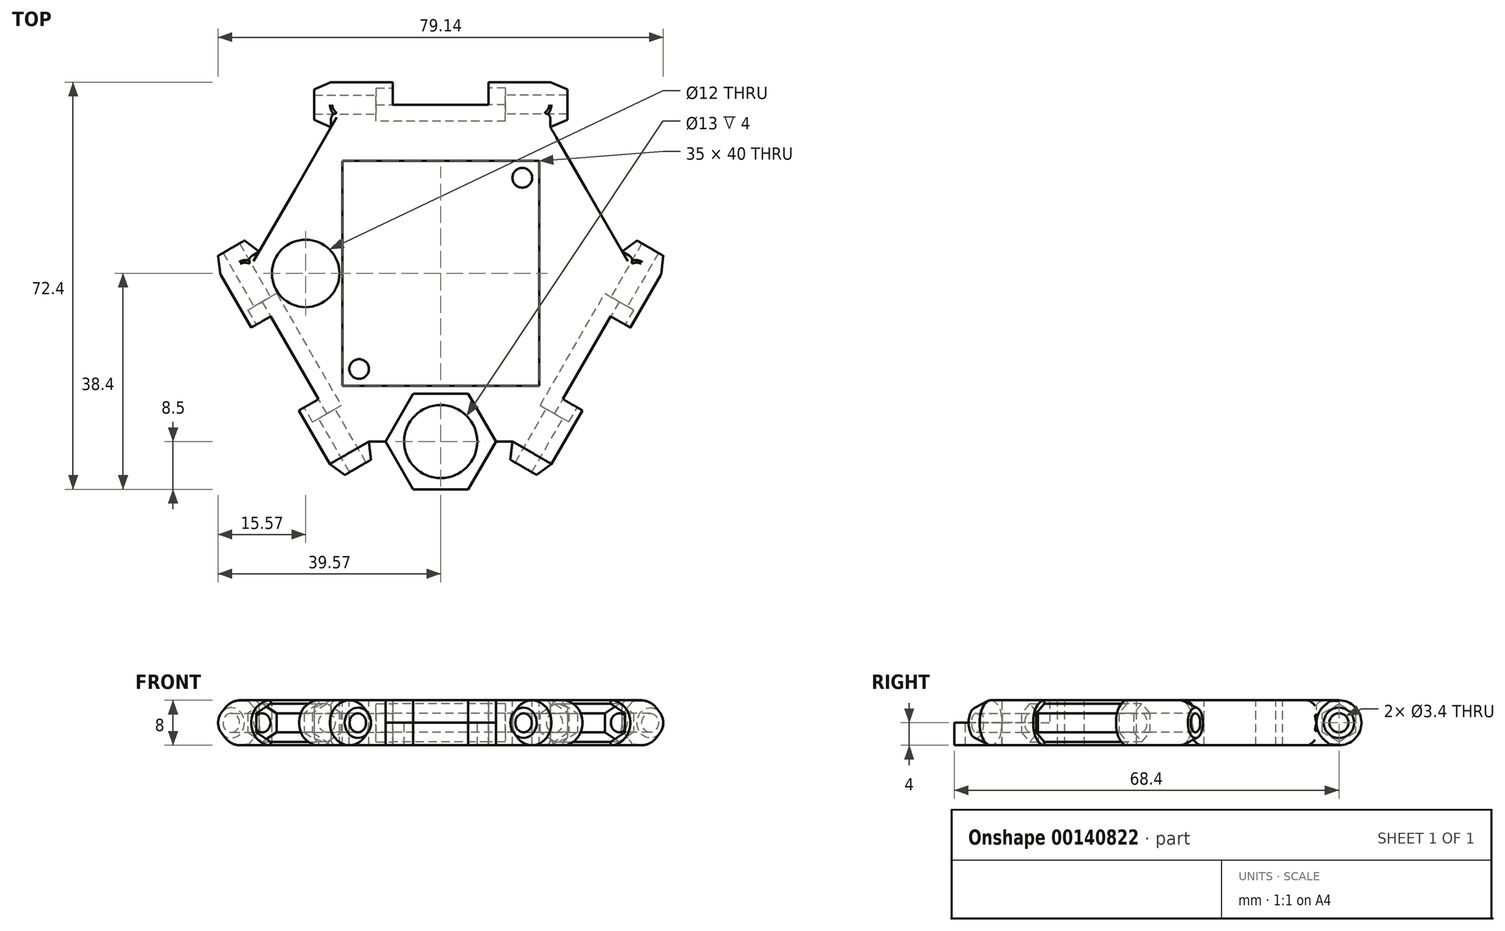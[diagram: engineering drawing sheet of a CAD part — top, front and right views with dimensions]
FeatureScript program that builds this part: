
annotation { "Feature Type Name" : "Feature", "Feature Type Description" : "" }
export const myFeature = defineFeature(function(context is Context, id is Id, definition is map)
    precondition{}
    {
        {
            var Q0;
            Q0=qCreatedBy(makeId("Top.planeOp"),FACE);
            var sketch = newSketch(context, id + "F0", { "sketchPlane" : qUnion([Q0])});
            skLineSegment(sketch, "E0.top", {"start": v(0, 34) * mm, "end": v(19.5, 34) * mm});
            skLineSegment(sketch, "E1", {"start": v(22.5, 31.7) * mm, "end": v(22.5, 32.7) * mm});
            skLineSegment(sketch, "E2", {"start": v(19.5, 34) * mm, "end": v(22.5, 32.7) * mm});
            skLineSegment(sketch, "E3", {"start": v(22.5, 31.7) * mm, "end": v(0, 31.7) * mm});
            skPoint(sketch, "E4.0.midPoint", {"position": v(0, 30) * mm});
            skLineSegment(sketch, "E5", {"start": v(19.5, 30) * mm, "end": v(36.82, 0) * mm, "construction": true});
            skLineSegment(sketch, "E6", {"start": v(0, 0) * mm, "end": v(27.62, 15.94) * mm, "construction": true});
            skLineSegment(sketch, "E7", {"start": v(0, 30) * mm, "end": v(22.5, 30) * mm, "construction": true});
            skLineSegment(sketch, "E8", {"start": v(0, 0) * mm, "end": v(0, 34) * mm});
            skLineSegment(sketch, "E9.MirrorCS", {"start": v(22.5, 28.3) * mm, "end": v(0, 28.3) * mm});
            skLineSegment(sketch, "E10.MirrorCS", {"start": v(0, 26) * mm, "end": v(19.5, 26) * mm});
            skLineSegment(sketch, "E11.MirrorCS", {"start": v(22.5, 28.3) * mm, "end": v(22.5, 27.3) * mm});
            skLineSegment(sketch, "E12.MirrorCS", {"start": v(19.5, 26) * mm, "end": v(22.5, 27.3) * mm});
            skLineSegment(sketch, "E13", {"start": v(19.5, 26) * mm, "end": v(32.2, 4) * mm, "construction": true});
            skLineSegment(sketch, "E14", {"start": v(0, 0) * mm, "end": v(25.88, 14.94) * mm});
            skLineSegment(sketch, "E15", {"start": v(19.5, 26) * mm, "end": v(25.88, 14.94) * mm});
            skSolve(sketch);
        }
        {
            var Q0;
            Q0=qCreatedBy(makeId("Right.planeOp"),FACE);
            var sketch = newSketch(context, id + "F1", { "sketchPlane" : qUnion([Q0])});
            skCircle(sketch, "E16.cCircle", {"center": v(30, 0) * mm, "radius": 2.95 * mm, "construction": true});
            skLineSegment(sketch, "E16.0", {"start": v(32.95, -1.7) * mm, "end": v(30, -3.4) * mm});
            skLineSegment(sketch, "E16.1", {"start": v(30, -3.4) * mm, "end": v(27.05, -1.7) * mm});
            skLineSegment(sketch, "E16.2", {"start": v(27.05, -1.7) * mm, "end": v(27.05, 1.7) * mm});
            skLineSegment(sketch, "E16.3", {"start": v(27.05, 1.7) * mm, "end": v(30, 3.4) * mm});
            skLineSegment(sketch, "E16.4", {"start": v(30, 3.4) * mm, "end": v(32.95, 1.7) * mm});
            skLineSegment(sketch, "E16.5", {"start": v(32.95, 1.7) * mm, "end": v(32.95, -1.7) * mm});
            skCircle(sketch, "E17", {"center": v(30, 0) * mm, "radius": 4 * mm});
            skLineSegment(sketch, "E18", {"start": v(26, 0) * mm, "end": v(26, -4) * mm});
            skLineSegment(sketch, "E19", {"start": v(26, -4) * mm, "end": v(30, -4) * mm});
            skLineSegment(sketch, "E20", {"start": v(30, 4) * mm, "end": v(30, -4) * mm, "construction": true});
            skLineSegment(sketch, "E21.MirrorCS", {"start": v(26, 4) * mm, "end": v(30, 4) * mm});
            skLineSegment(sketch, "E22.MirrorCS", {"start": v(26, 0) * mm, "end": v(26, 4) * mm});
            skLineSegment(sketch, "E23", {"start": v(0, 4) * mm, "end": v(0, -4) * mm, "construction": true});
            skLineSegment(sketch, "E24", {"start": v(30, 4) * mm, "end": v(30, 3.4) * mm});
            skLineSegment(sketch, "E25", {"start": v(30, -3.4) * mm, "end": v(30, -4) * mm});
            skSolve(sketch);
        }
        {
            var Q0;
            Q0=qCreatedBy(makeId("Top.planeOp"),FACE);
            var sketch = newSketch(context, id + "F2", { "sketchPlane" : qUnion([Q0])});
            skCircle(sketch, "E26.MirrorC", {"center": v(14.5, 17) * mm, "radius": 1.75 * mm});
            skLineSegment(sketch, "E27", {"start": v(0, 20) * mm, "end": v(17.5, 20) * mm, "construction": true});
            skLineSegment(sketch, "E28", {"start": v(17.5, 20) * mm, "end": v(17.5, 0) * mm, "construction": true});
            skLineSegment(sketch, "E29", {"start": v(17.5, 20) * mm, "end": v(0, 0) * mm, "construction": true});
            skCircle(sketch, "E30", {"center": v(10, 10) * mm, "radius": 4 * mm, "construction": true});
            skLineSegment(sketch, "E31", {"start": v(0, 10) * mm, "end": v(17.5, 10) * mm, "construction": true});
            skFitSpline(sketch, "E32", {"points": [v(12.53, 14.32) * mm, v(14.26, 12.62) * mm, v(15, 10) * mm], "startDerivative": vector(4.86, -2.41) * mm, "endDerivative": vector(0.41, -5.85) * mm});
            skLineSegment(sketch, "E33", {"start": v(15, 10) * mm, "end": v(15, 0) * mm});
            skLineSegment(sketch, "E34", {"start": v(12.53, 14.32) * mm, "end": v(2.46, 16.87) * mm});
            skLineSegment(sketch, "E35.MirrorCS", {"start": v(-12.53, 14.32) * mm, "end": v(-2.46, 16.87) * mm});
            skFitSpline(sketch, "E36.MirrorCS", {"points": [v(-12.53, 14.32) * mm, v(-14.26, 12.62) * mm, v(-15, 10) * mm], "startDerivative": vector(-4.86, -2.41) * mm, "endDerivative": vector(-0.41, -5.85) * mm});
            skLineSegment(sketch, "E37.MirrorCS", {"start": v(-15, 10) * mm, "end": v(-15, 0) * mm});
            skCircle(sketch, "E38.MirrorC", {"center": v(-14.5, 17) * mm, "radius": 1.75 * mm});
            skPoint(sketch, "E39.visualSharp", {"position": v(0, 17.5) * mm});
            skArc(sketch, "E39.filletArc", {"start": v(2.46, 16.87) * mm, "mid": v(0, 17.18) * mm, "end": v(-2.46, 16.87) * mm});
            skCircle(sketch, "E40.MirrorC", {"center": v(-14.5, -17) * mm, "radius": 1.75 * mm});
            skCircle(sketch, "E41.MirrorC", {"center": v(14.5, -17) * mm, "radius": 1.75 * mm});
            skLineSegment(sketch, "E42.MirrorCS", {"start": v(15, -10) * mm, "end": v(15, 0) * mm});
            skFitSpline(sketch, "E43.MirrorCS", {"points": [v(12.53, -14.32) * mm, v(14.26, -12.62) * mm, v(15, -10) * mm], "startDerivative": vector(4.86, 2.41) * mm, "endDerivative": vector(0.41, 5.85) * mm});
            skLineSegment(sketch, "E44.MirrorCS", {"start": v(12.53, -14.32) * mm, "end": v(2.46, -16.87) * mm});
            skArc(sketch, "E45.MirrorCS", {"start": v(2.46, -16.87) * mm, "mid": v(0, -17.18) * mm, "end": v(-2.46, -16.87) * mm});
            skLineSegment(sketch, "E46.MirrorCS", {"start": v(-12.53, -14.32) * mm, "end": v(-2.46, -16.87) * mm});
            skLineSegment(sketch, "E47.MirrorCS", {"start": v(-15, -10) * mm, "end": v(-15, 0) * mm});
            skFitSpline(sketch, "E48.MirrorCS", {"points": [v(-12.53, -14.32) * mm, v(-14.26, -12.62) * mm, v(-15, -10) * mm], "startDerivative": vector(-4.86, 2.41) * mm, "endDerivative": vector(-0.41, 5.85) * mm});
            skLineSegment(sketch, "E49.bottom", {"start": v(-17.5, 20) * mm, "end": v(17.5, 20) * mm});
            skLineSegment(sketch, "E49.top", {"start": v(-17.5, -20) * mm, "end": v(17.5, -20) * mm});
            skLineSegment(sketch, "E49.left", {"start": v(-17.5, 20) * mm, "end": v(-17.5, -20) * mm});
            skLineSegment(sketch, "E49.right", {"start": v(17.5, 20) * mm, "end": v(17.5, -20) * mm});
            skPoint(sketch, "E49.middle", {"position": v(0, 0) * mm});
            skCircle(sketch, "E50", {"center": v(-24, 0) * mm, "radius": 6 * mm});
            skCircle(sketch, "E51.MirrorC", {"center": v(24, 0) * mm, "radius": 6 * mm});
            skSolve(sketch);
        }
        {
            var Q0;
            {var subQ1=sQuery(id+"F0.wireOp",EDGE,"E0.top");Q0=makeQuery(id+"F0.imprint","IMPRINT",FACE,{"disambiguationData":[TD([[makeQuery(id+"F0.imprint","IMPRINT",EDGE,{"derivedFrom":subQ1}),-1.0]])]});}
            var Q1;
            Q1=sQuery(id+"F0.wireOp",EDGE,"E7");
            revolve(context, id + "F3", {"entities" : qUnion([Q0]), "axis" : qUnion([Q1]), "revolveType" : RevolveType.FULL});
        }
        {
            var Q0;
            {var subQ2=sQuery(id+"F1.wireOp",EDGE,"E21.MirrorCS");Q0=makeQuery(id+"F1.imprint","IMPRINT",FACE,{"disambiguationData":[TD([[makeQuery(id+"F1.imprint","IMPRINT",EDGE,{"derivedFrom":subQ2}),-1.0]])]});}
            var Q1;
            {var subQ0=sQuery(id+"F1.wireOp",EDGE,"E18");Q1=makeQuery(id+"F1.imprint","IMPRINT",FACE,{"disambiguationData":[TD([[makeQuery(id+"F1.imprint","IMPRINT",EDGE,{"derivedFrom":subQ0}),1.0]])]});}
            var Q2;
            {var subQ0=sQuery(id+"F1.wireOp",EDGE,"E19");var subQ1=sQuery(id+"F1.wireOp",EDGE,"E17");var subQ2=makeQuery(id+"F1.imprint","INTERSECT",VERTEX,{"derivedFrom":[subQ1,subQ0]});Q2=makeQuery(id+"F1.imprint","IMPRINT",FACE,{"disambiguationData":[TD([[makeQuery(id+"F1.imprint","IMPRINT",EDGE,{"disambiguationData":[TD([[subQ2,1.0]])],"derivedFrom":subQ1}),-1.0]])]});}
            var Q3;
            {var subQ0=sQuery(id+"F1.wireOp",EDGE,"E22.MirrorCS");Q3=makeQuery(id+"F1.imprint","IMPRINT",FACE,{"disambiguationData":[TD([[makeQuery(id+"F1.imprint","IMPRINT",EDGE,{"derivedFrom":subQ0}),-1.0]])]});}
            extrude(context, id + "F4", {"entities" : qUnion([Q0, Q1, Q2, Q3]), "operationType" : NewBodyOperationType.ADD, "depth" : 19.5 * mm});
        }
        {
            var Q0;
            {var subQ2=sQuery(id+"F0.wireOp",EDGE,"E10.MirrorCS");Q0=makeQuery(id+"F0.imprint","IMPRINT",FACE,{"disambiguationData":[TD([[makeQuery(id+"F0.imprint","IMPRINT",EDGE,{"derivedFrom":subQ2}),-1.0]])]});}
            extrude(context, id + "F5", {"entities" : qUnion([Q0]), "operationType" : NewBodyOperationType.ADD, "endBound" : BoundingType.SYMMETRIC, "depth" : 8 * mm});
        }
        {
            var Q0;
            Q0=makeQuery(id+"F1.imprint","IMPRINT",FACE,{"disambiguationData":[TD([[makeQuery(id+"F1.imprint","IMPRINT",EDGE,{"derivedFrom":sQuery(id+"F1.wireOp",EDGE,"E16.0")}),-1.0]])]});
            extrude(context, id + "F6", {"entities" : qUnion([Q0]), "operationType" : NewBodyOperationType.REMOVE, "depth" : (45 / 2 - 11) * mm});
        }
        {
            var Q0;
            Q0=makeQuery(id+"F1.imprint","IMPRINT",FACE,{"disambiguationData":[TD([[makeQuery(id+"F1.imprint","IMPRINT",EDGE,{"derivedFrom":sQuery(id+"F1.wireOp",EDGE,"E16.0")}),1.0]])]});
            extrude(context, id + "F7", {"entities" : qUnion([Q0]), "operationType" : NewBodyOperationType.REMOVE, "depth" : (45 / 2 - 14) * mm});
        }
        {
            var Q0;
            Q0=makeQuery(id+"F3.opRevolve","SWEPT_BODY",BODY,{"disambiguationData":[OSD([sQuery(id+"F0.wireOp",EDGE,"E0.top"),sQuery(id+"F0.wireOp",EDGE,"E0.left"),sQuery(id+"F0.wireOp",EDGE,"E1"),sQuery(id+"F0.wireOp",EDGE,"E2"),sQuery(id+"F0.wireOp",EDGE,"E3")])]});
            var Q1;
            Q1=qCreatedBy(makeId("Right.planeOp"),FACE);
            mirror(context, id + "F8", {"operationType" : NewBodyOperationType.ADD, "entities" : qUnion([Q0]), "mirrorPlane" : qUnion([Q1])});
        }
        {
            var Q0;
            Q0=makeQuery(id+"F3.opRevolve","SWEPT_BODY",BODY,{"disambiguationData":[OSD([sQuery(id+"F0.wireOp",EDGE,"E0.top"),sQuery(id+"F0.wireOp",EDGE,"E0.left"),sQuery(id+"F0.wireOp",EDGE,"E1"),sQuery(id+"F0.wireOp",EDGE,"E2"),sQuery(id+"F0.wireOp",EDGE,"E3")])]});
            var Q1;
            Q1=makeQuery(id+"F3.opRevolve","SWEPT_BODY",BODY,{"disambiguationData":[OSD([sQuery(id+"F0.wireOp",EDGE,"E8"),sQuery(id+"F0.wireOp",EDGE,"E9.MirrorCS"),sQuery(id+"F0.wireOp",EDGE,"E10.MirrorCS"),sQuery(id+"F0.wireOp",EDGE,"E11.MirrorCS"),sQuery(id+"F0.wireOp",EDGE,"E12.MirrorCS")])]});
            var Q2;
            Q2=sQuery(id+"F1.wireOp",EDGE,"E23");
            circularPattern(context, id + "F9", {"operationType" : NewBodyOperationType.ADD, "entities" : qUnion([Q0, Q1]), "axis" : qUnion([Q2]), "angle" : 120 * degree, "instanceCount" : 3});
        }
        {
            var Q0;
            Q0=makeQuery(id+"F2.imprint","IMPRINT",FACE,{"disambiguationData":[TD([[makeQuery(id+"F2.imprint","IMPRINT",EDGE,{"derivedFrom":sQuery(id+"F2.wireOp",EDGE,"E32")}),-1.0]])]});
            var Q1;
            Q1=makeQuery(id+"F2.imprint","IMPRINT",FACE,{"disambiguationData":[TD([[makeQuery(id+"F2.imprint","IMPRINT",EDGE,{"derivedFrom":sQuery(id+"F2.wireOp",EDGE,"E38.MirrorC")}),1.0]])]});
            var Q2;
            Q2=makeQuery(id+"F2.imprint","IMPRINT",FACE,{"disambiguationData":[TD([[makeQuery(id+"F2.imprint","IMPRINT",EDGE,{"derivedFrom":sQuery(id+"F2.wireOp",EDGE,"E26.MirrorC")}),-1.0]])]});
            var Q3;
            Q3=makeQuery(id+"F2.imprint","IMPRINT",FACE,{"disambiguationData":[TD([[makeQuery(id+"F2.imprint","IMPRINT",EDGE,{"derivedFrom":sQuery(id+"F2.wireOp",EDGE,"E41.MirrorC")}),1.0]])]});
            var Q4;
            Q4=makeQuery(id+"F2.imprint","IMPRINT",FACE,{"disambiguationData":[TD([[makeQuery(id+"F2.imprint","IMPRINT",EDGE,{"derivedFrom":sQuery(id+"F2.wireOp",EDGE,"E40.MirrorC")}),-1.0]])]});
            var Q5;
            Q5=makeQuery(id+"F2.imprint","IMPRINT",FACE,{"disambiguationData":[TD([[makeQuery(id+"F2.imprint","IMPRINT",EDGE,{"derivedFrom":sQuery(id+"F2.wireOp",EDGE,"E50")}),1.0]])]});
            var Q6;
            Q6=makeQuery(id+"F2.imprint","IMPRINT",FACE,{"disambiguationData":[TD([[makeQuery(id+"F2.imprint","IMPRINT",EDGE,{"derivedFrom":sQuery(id+"F2.wireOp",EDGE,"E51.MirrorC")}),-1.0]])]});
            var Q7;
            {var subQ0=sQuery(id+"F2.wireOp",EDGE,"E50");var subQ1=sQuery(id+"F2.wireOp",EDGE,"JJTMQ2RY-KDWr-5WRS-YdwC-lt0RPVDN6D57.right");var subQ2=makeQuery(id+"F2.imprint","INTERSECT",VERTEX,{"disambiguationData":[OD(0.0)],"derivedFrom":[subQ1,subQ0]});Q7=makeQuery(id+"F2.imprint","IMPRINT",FACE,{"disambiguationData":[TD([[makeQuery(id+"F2.imprint","IMPRINT",EDGE,{"disambiguationData":[TD([[subQ2,-1.0]])],"derivedFrom":subQ1}),1.0]])]});}
            var Q8;
            {var subQ0=sQuery(id+"F2.wireOp",EDGE,"E51.MirrorC");var subQ1=sQuery(id+"F2.wireOp",EDGE,"JJTMQ2RY-KDWr-5WRS-YdwC-lt0RPVDN6D57.left");var subQ2=makeQuery(id+"F2.imprint","INTERSECT",VERTEX,{"disambiguationData":[OD(0.0)],"derivedFrom":[subQ1,subQ0]});Q8=makeQuery(id+"F2.imprint","IMPRINT",FACE,{"disambiguationData":[TD([[makeQuery(id+"F2.imprint","IMPRINT",EDGE,{"disambiguationData":[TD([[subQ2,-1.0]])],"derivedFrom":subQ1}),-1.0]])]});}
            extrude(context, id + "F10", {"entities" : qUnion([Q0, Q1, Q2, Q3, Q4, Q5, Q6, Q7, Q8]), "operationType" : NewBodyOperationType.REMOVE, "endBound" : BoundingType.SYMMETRIC, "oppositeDirection" : true, "depth" : 8 * mm});
        }
        {
            var Q0;
            Q0=qCreatedBy(makeId("Top.planeOp"),FACE);
            var sketch = newSketch(context, id + "F11", { "sketchPlane" : qUnion([Q0])});
            skCircle(sketch, "E52.cCircle", {"center": v(0, -29.9) * mm, "radius": 8.5 * mm, "construction": true});
            skLineSegment(sketch, "E52.0", {"start": v(-4.9, -21.4) * mm, "end": v(4.9, -21.4) * mm});
            skLineSegment(sketch, "E52.1", {"start": v(4.9, -21.4) * mm, "end": v(9.81, -29.9) * mm});
            skLineSegment(sketch, "E52.2", {"start": v(9.81, -29.9) * mm, "end": v(4.9, -38.4) * mm});
            skLineSegment(sketch, "E52.3", {"start": v(4.9, -38.4) * mm, "end": v(-4.9, -38.4) * mm});
            skLineSegment(sketch, "E52.4", {"start": v(-4.9, -38.4) * mm, "end": v(-9.81, -29.9) * mm});
            skLineSegment(sketch, "E52.5", {"start": v(-9.81, -29.9) * mm, "end": v(-4.9, -21.4) * mm});
            skPoint(sketch, "E52.0.midPoint", {"position": v(0, -21.4) * mm});
            skCircle(sketch, "E53", {"center": v(0, -29.9) * mm, "radius": 6.5 * mm});
            skCircle(sketch, "E54", {"center": v(0, -29.9) * mm, "radius": 10 * mm});
            skSolve(sketch);
        }
        {
            var Q0;
            Q0=makeQuery(id+"F11.imprint","IMPRINT",FACE,{"disambiguationData":[TD([[makeQuery(id+"F11.imprint","IMPRINT",EDGE,{"derivedFrom":sQuery(id+"F11.wireOp",EDGE,"E53")}),1.0]])]});
            var Q1;
            Q1=makeQuery(id+"F11.imprint","IMPRINT",FACE,{"disambiguationData":[TD([[makeQuery(id+"F11.imprint","IMPRINT",EDGE,{"derivedFrom":sQuery(id+"F11.wireOp",EDGE,"E52.0")}),-1.0]])]});
            extrude(context, id + "F12", {"entities" : qUnion([Q0, Q1]), "operationType" : NewBodyOperationType.REMOVE, "endBound" : BoundingType.SYMMETRIC, "depth" : 40 * mm});
        }
        {
            var Q0;
            Q0=makeQuery(id+"F11.imprint","IMPRINT",FACE,{"disambiguationData":[TD([[makeQuery(id+"F11.imprint","IMPRINT",EDGE,{"derivedFrom":sQuery(id+"F11.wireOp",EDGE,"E52.0")}),-1.0]])]});
            extrude(context, id + "F13", {"entities" : qUnion([Q0]), "operationType" : NewBodyOperationType.ADD, "oppositeDirection" : true, "depth" : 4 * mm});
        }
        {
            var Q0;
            {var subQ0=makeQuery(id+"F5.opExtrude","CAP_EDGE",EDGE,{"disambiguationData":[OSD([sQuery(id+"F0.wireOp",EDGE,"E15")])],"isStart":false});Q0=makeQuery(id+"F9.boolean.opBoolean","MERGE",EDGE,{"derivedFrom":[subQ0,makeQuery(id+"F9.opPattern","COPY",EDGE,{"derivedFrom":makeQuery(id+"F8.opPattern","COPY",EDGE,{"derivedFrom":subQ0,"instanceName":"1"}),"instanceName":"1"})]});}
            var Q1;
            {var subQ0=makeQuery(id+"F5.opExtrude","CAP_EDGE",EDGE,{"disambiguationData":[OSD([sQuery(id+"F0.wireOp",EDGE,"E15")])],"isStart":true});Q1=makeQuery(id+"F9.boolean.opBoolean","MERGE",EDGE,{"derivedFrom":[subQ0,makeQuery(id+"F9.opPattern","COPY",EDGE,{"derivedFrom":makeQuery(id+"F8.opPattern","COPY",EDGE,{"derivedFrom":subQ0,"instanceName":"1"}),"instanceName":"1"})]});}
            var Q2;
            Q2=makeQuery(id+"F9.opPattern","COPY",EDGE,{"derivedFrom":makeQuery(id+"F8.opPattern","COPY",EDGE,{"derivedFrom":makeQuery(id+"F4.opExtrude","CAP_EDGE",EDGE,{"disambiguationData":[OSD([sQuery(id+"F1.wireOp",EDGE,"E21.MirrorCS")])],"isStart":false}),"instanceName":"1"}),"instanceName":"1"});
            var Q3;
            Q3=makeQuery(id+"F9.opPattern","COPY",EDGE,{"derivedFrom":makeQuery(id+"F8.opPattern","COPY",EDGE,{"derivedFrom":makeQuery(id+"F4.opExtrude","CAP_EDGE",EDGE,{"disambiguationData":[OSD([sQuery(id+"F1.wireOp",EDGE,"E19")])],"isStart":false}),"instanceName":"1"}),"instanceName":"1"});
            var Q4;
            Q4=makeQuery(id+"F4.opExtrude","CAP_EDGE",EDGE,{"disambiguationData":[OSD([sQuery(id+"F1.wireOp",EDGE,"E19")])],"isStart":false});
            var Q5;
            Q5=makeQuery(id+"F4.opExtrude","CAP_EDGE",EDGE,{"disambiguationData":[OSD([sQuery(id+"F1.wireOp",EDGE,"E21.MirrorCS")])],"isStart":false});
            var Q6;
            {var subQ0=makeQuery(id+"F5.opExtrude","CAP_EDGE",EDGE,{"disambiguationData":[OSD([sQuery(id+"F0.wireOp",EDGE,"E15")])],"isStart":false});Q6=makeQuery(id+"F9.boolean.opBoolean","MERGE",EDGE,{"derivedFrom":[makeQuery(id+"F8.opPattern","COPY",EDGE,{"derivedFrom":subQ0,"instanceName":"1"}),makeQuery(id+"F9.opPattern","COPY",EDGE,{"derivedFrom":subQ0,"instanceName":"2"})]});}
            var Q7;
            Q7=makeQuery(id+"F8.opPattern","COPY",EDGE,{"derivedFrom":makeQuery(id+"F4.opExtrude","CAP_EDGE",EDGE,{"disambiguationData":[OSD([sQuery(id+"F1.wireOp",EDGE,"E21.MirrorCS")])],"isStart":false}),"instanceName":"1"});
            var Q8;
            Q8=makeQuery(id+"F9.opPattern","COPY",EDGE,{"derivedFrom":makeQuery(id+"F4.opExtrude","CAP_EDGE",EDGE,{"disambiguationData":[OSD([sQuery(id+"F1.wireOp",EDGE,"E21.MirrorCS")])],"isStart":false}),"instanceName":"2"});
            var Q9;
            Q9=makeQuery(id+"F9.opPattern","COPY",EDGE,{"derivedFrom":makeQuery(id+"F4.opExtrude","CAP_EDGE",EDGE,{"disambiguationData":[OSD([sQuery(id+"F1.wireOp",EDGE,"E19")])],"isStart":false}),"instanceName":"2"});
            var Q10;
            {var subQ0=makeQuery(id+"F5.opExtrude","CAP_EDGE",EDGE,{"disambiguationData":[OSD([sQuery(id+"F0.wireOp",EDGE,"E15")])],"isStart":true});Q10=makeQuery(id+"F9.boolean.opBoolean","MERGE",EDGE,{"derivedFrom":[makeQuery(id+"F8.opPattern","COPY",EDGE,{"derivedFrom":subQ0,"instanceName":"1"}),makeQuery(id+"F9.opPattern","COPY",EDGE,{"derivedFrom":subQ0,"instanceName":"2"})]});}
            var Q11;
            Q11=makeQuery(id+"F8.opPattern","COPY",EDGE,{"derivedFrom":makeQuery(id+"F4.opExtrude","CAP_EDGE",EDGE,{"disambiguationData":[OSD([sQuery(id+"F1.wireOp",EDGE,"E19")])],"isStart":false}),"instanceName":"1"});
            var Q12;
            Q12=makeQuery(id+"F9.opPattern","COPY",EDGE,{"derivedFrom":makeQuery(id+"F5.boolean.opBoolean","MERGE",EDGE,{"derivedFrom":[makeQuery(id+"F4.opExtrude","CAP_EDGE",EDGE,{"disambiguationData":[OSD([sQuery(id+"F1.wireOp",EDGE,"E18")])],"isStart":false}),makeQuery(id+"F5.opExtrude","SWEPT_EDGE",EDGE,{"disambiguationData":[OSD([sQuery(id+"F0.wireOp",EDGE,"E10.MirrorCS"),sQuery(id+"F0.wireOp",EDGE,"E12.MirrorCS"),sQuery(id+"F0.wireOp",EDGE,"E15")])]})]}),"instanceName":"2"});
            var Q13;
            Q13=makeQuery(id+"F8.opPattern","COPY",EDGE,{"derivedFrom":makeQuery(id+"F5.boolean.opBoolean","MERGE",EDGE,{"derivedFrom":[makeQuery(id+"F4.opExtrude","CAP_EDGE",EDGE,{"disambiguationData":[OSD([sQuery(id+"F1.wireOp",EDGE,"E18")])],"isStart":false}),makeQuery(id+"F5.opExtrude","SWEPT_EDGE",EDGE,{"disambiguationData":[OSD([sQuery(id+"F0.wireOp",EDGE,"E10.MirrorCS"),sQuery(id+"F0.wireOp",EDGE,"E12.MirrorCS"),sQuery(id+"F0.wireOp",EDGE,"E15")])]})]}),"instanceName":"1"});
            var Q14;
            Q14=makeQuery(id+"F5.boolean.opBoolean","MERGE",EDGE,{"derivedFrom":[makeQuery(id+"F4.opExtrude","CAP_EDGE",EDGE,{"disambiguationData":[OSD([sQuery(id+"F1.wireOp",EDGE,"E22.MirrorCS")])],"isStart":false}),makeQuery(id+"F5.opExtrude","SWEPT_EDGE",EDGE,{"disambiguationData":[OSD([sQuery(id+"F0.wireOp",EDGE,"E10.MirrorCS"),sQuery(id+"F0.wireOp",EDGE,"E12.MirrorCS"),sQuery(id+"F0.wireOp",EDGE,"E15")])]})]});
            var Q15;
            Q15=makeQuery(id+"F5.boolean.opBoolean","MERGE",EDGE,{"derivedFrom":[makeQuery(id+"F4.opExtrude","CAP_EDGE",EDGE,{"disambiguationData":[OSD([sQuery(id+"F1.wireOp",EDGE,"E18")])],"isStart":false}),makeQuery(id+"F5.opExtrude","SWEPT_EDGE",EDGE,{"disambiguationData":[OSD([sQuery(id+"F0.wireOp",EDGE,"E10.MirrorCS"),sQuery(id+"F0.wireOp",EDGE,"E12.MirrorCS"),sQuery(id+"F0.wireOp",EDGE,"E15")])]})]});
            var Q16;
            Q16=makeQuery(id+"F9.opPattern","COPY",EDGE,{"derivedFrom":makeQuery(id+"F8.opPattern","COPY",EDGE,{"derivedFrom":makeQuery(id+"F5.boolean.opBoolean","MERGE",EDGE,{"derivedFrom":[makeQuery(id+"F4.opExtrude","CAP_EDGE",EDGE,{"disambiguationData":[OSD([sQuery(id+"F1.wireOp",EDGE,"E18")])],"isStart":false}),makeQuery(id+"F5.opExtrude","SWEPT_EDGE",EDGE,{"disambiguationData":[OSD([sQuery(id+"F0.wireOp",EDGE,"E10.MirrorCS"),sQuery(id+"F0.wireOp",EDGE,"E12.MirrorCS"),sQuery(id+"F0.wireOp",EDGE,"E15")])]})]}),"instanceName":"1"}),"instanceName":"1"});
            var Q17;
            Q17=makeQuery(id+"F9.opPattern","COPY",EDGE,{"derivedFrom":makeQuery(id+"F5.boolean.opBoolean","MERGE",EDGE,{"derivedFrom":[makeQuery(id+"F4.opExtrude","CAP_EDGE",EDGE,{"disambiguationData":[OSD([sQuery(id+"F1.wireOp",EDGE,"E22.MirrorCS")])],"isStart":false}),makeQuery(id+"F5.opExtrude","SWEPT_EDGE",EDGE,{"disambiguationData":[OSD([sQuery(id+"F0.wireOp",EDGE,"E10.MirrorCS"),sQuery(id+"F0.wireOp",EDGE,"E12.MirrorCS"),sQuery(id+"F0.wireOp",EDGE,"E15")])]})]}),"instanceName":"1"});
            var Q18;
            Q18=makeQuery(id+"F9.opPattern","COPY",EDGE,{"derivedFrom":makeQuery(id+"F5.boolean.opBoolean","MERGE",EDGE,{"derivedFrom":[makeQuery(id+"F4.opExtrude","CAP_EDGE",EDGE,{"disambiguationData":[OSD([sQuery(id+"F1.wireOp",EDGE,"E18")])],"isStart":false}),makeQuery(id+"F5.opExtrude","SWEPT_EDGE",EDGE,{"disambiguationData":[OSD([sQuery(id+"F0.wireOp",EDGE,"E10.MirrorCS"),sQuery(id+"F0.wireOp",EDGE,"E12.MirrorCS"),sQuery(id+"F0.wireOp",EDGE,"E15")])]})]}),"instanceName":"1"});
            var Q19;
            Q19=makeQuery(id+"F9.opPattern","COPY",EDGE,{"derivedFrom":makeQuery(id+"F8.opPattern","COPY",EDGE,{"derivedFrom":makeQuery(id+"F5.boolean.opBoolean","MERGE",EDGE,{"derivedFrom":[makeQuery(id+"F4.opExtrude","CAP_EDGE",EDGE,{"disambiguationData":[OSD([sQuery(id+"F1.wireOp",EDGE,"E18")])],"isStart":false}),makeQuery(id+"F5.opExtrude","SWEPT_EDGE",EDGE,{"disambiguationData":[OSD([sQuery(id+"F0.wireOp",EDGE,"E10.MirrorCS"),sQuery(id+"F0.wireOp",EDGE,"E12.MirrorCS"),sQuery(id+"F0.wireOp",EDGE,"E15")])]})]}),"instanceName":"1"}),"instanceName":"2"});
            var Q20;
            Q20=makeQuery(id+"F10.boolean.opBoolean","COPY",EDGE,{"derivedFrom":makeQuery(id+"F10.opExtrude","CAP_EDGE",EDGE,{"disambiguationData":[OSD([sQuery(id+"F2.wireOp",EDGE,"E37.MirrorCS"),sQuery(id+"F2.wireOp",EDGE,"E47.MirrorCS")])],"isStart":true})});
            var Q21;
            Q21=makeQuery(id+"F10.boolean.opBoolean","COPY",EDGE,{"derivedFrom":makeQuery(id+"F10.opExtrude","CAP_EDGE",EDGE,{"disambiguationData":[OSD([sQuery(id+"F2.wireOp",EDGE,"E37.MirrorCS"),sQuery(id+"F2.wireOp",EDGE,"E47.MirrorCS")])],"isStart":false})});
            var Q22;
            Q22=makeQuery(id+"F10.boolean.opBoolean","COPY",EDGE,{"derivedFrom":makeQuery(id+"F10.opExtrude","CAP_EDGE",EDGE,{"disambiguationData":[OSD([sQuery(id+"F2.wireOp",EDGE,"E33"),sQuery(id+"F2.wireOp",EDGE,"E42.MirrorCS")])],"isStart":true})});
            var Q23;
            Q23=makeQuery(id+"F10.boolean.opBoolean","COPY",EDGE,{"derivedFrom":makeQuery(id+"F10.opExtrude","CAP_EDGE",EDGE,{"disambiguationData":[OSD([sQuery(id+"F2.wireOp",EDGE,"E39.filletArc")])],"isStart":true})});
            var Q24;
            Q24=makeQuery(id+"F10.boolean.opBoolean","COPY",EDGE,{"derivedFrom":makeQuery(id+"F10.opExtrude","CAP_EDGE",EDGE,{"disambiguationData":[OSD([sQuery(id+"F2.wireOp",EDGE,"E39.filletArc")])],"isStart":false})});
            var Q25;
            Q25=makeQuery(id+"F10.boolean.opBoolean","COPY",EDGE,{"derivedFrom":makeQuery(id+"F10.opExtrude","CAP_EDGE",EDGE,{"disambiguationData":[OSD([sQuery(id+"F2.wireOp",EDGE,"E32")])],"isStart":true})});
            var Q26;
            Q26=makeQuery(id+"F10.boolean.opBoolean","COPY",EDGE,{"derivedFrom":makeQuery(id+"F10.opExtrude","CAP_EDGE",EDGE,{"disambiguationData":[OSD([sQuery(id+"F2.wireOp",EDGE,"E43.MirrorCS")])],"isStart":true})});
            var Q27;
            Q27=makeQuery(id+"F10.boolean.opBoolean","COPY",EDGE,{"derivedFrom":makeQuery(id+"F10.opExtrude","CAP_EDGE",EDGE,{"disambiguationData":[OSD([sQuery(id+"F2.wireOp",EDGE,"E48.MirrorCS")])],"isStart":true})});
            var Q28;
            Q28=makeQuery(id+"F10.boolean.opBoolean","COPY",EDGE,{"derivedFrom":makeQuery(id+"F10.opExtrude","CAP_EDGE",EDGE,{"disambiguationData":[OSD([sQuery(id+"F2.wireOp",EDGE,"E46.MirrorCS")])],"isStart":true})});
            var Q29;
            Q29=makeQuery(id+"F10.boolean.opBoolean","COPY",EDGE,{"derivedFrom":makeQuery(id+"F10.opExtrude","CAP_EDGE",EDGE,{"disambiguationData":[OSD([sQuery(id+"F2.wireOp",EDGE,"E36.MirrorCS")])],"isStart":true})});
            var Q30;
            Q30=makeQuery(id+"F10.boolean.opBoolean","COPY",EDGE,{"derivedFrom":makeQuery(id+"F10.opExtrude","CAP_EDGE",EDGE,{"disambiguationData":[OSD([sQuery(id+"F2.wireOp",EDGE,"E36.MirrorCS")])],"isStart":false})});
            var Q31;
            Q31=makeQuery(id+"F10.boolean.opBoolean","COPY",EDGE,{"derivedFrom":makeQuery(id+"F10.opExtrude","CAP_EDGE",EDGE,{"disambiguationData":[OSD([sQuery(id+"F2.wireOp",EDGE,"E35.MirrorCS")])],"isStart":true})});
            var Q32;
            Q32=makeQuery(id+"F10.boolean.opBoolean","COPY",EDGE,{"derivedFrom":makeQuery(id+"F10.opExtrude","CAP_EDGE",EDGE,{"disambiguationData":[OSD([sQuery(id+"F2.wireOp",EDGE,"E34")])],"isStart":true})});
            var Q33;
            Q33=makeQuery(id+"F10.boolean.opBoolean","COPY",EDGE,{"derivedFrom":makeQuery(id+"F10.opExtrude","CAP_EDGE",EDGE,{"disambiguationData":[OSD([sQuery(id+"F2.wireOp",EDGE,"E35.MirrorCS")])],"isStart":false})});
            var Q34;
            Q34=makeQuery(id+"F10.boolean.opBoolean","COPY",EDGE,{"derivedFrom":makeQuery(id+"F10.opExtrude","CAP_EDGE",EDGE,{"disambiguationData":[OSD([sQuery(id+"F2.wireOp",EDGE,"E44.MirrorCS")])],"isStart":false})});
            var Q35;
            Q35=makeQuery(id+"F10.boolean.opBoolean","COPY",EDGE,{"derivedFrom":makeQuery(id+"F10.opExtrude","CAP_EDGE",EDGE,{"disambiguationData":[OSD([sQuery(id+"F2.wireOp",EDGE,"E45.MirrorCS")])],"isStart":false})});
            var Q36;
            Q36=makeQuery(id+"F10.boolean.opBoolean","COPY",EDGE,{"derivedFrom":makeQuery(id+"F10.opExtrude","CAP_EDGE",EDGE,{"disambiguationData":[OSD([sQuery(id+"F2.wireOp",EDGE,"E46.MirrorCS")])],"isStart":false})});
            var Q37;
            Q37=makeQuery(id+"F10.boolean.opBoolean","COPY",EDGE,{"derivedFrom":makeQuery(id+"F10.opExtrude","CAP_EDGE",EDGE,{"disambiguationData":[OSD([sQuery(id+"F2.wireOp",EDGE,"E48.MirrorCS")])],"isStart":false})});
            var Q38;
            Q38=makeQuery(id+"F10.boolean.opBoolean","COPY",EDGE,{"derivedFrom":makeQuery(id+"F10.opExtrude","CAP_EDGE",EDGE,{"disambiguationData":[OSD([sQuery(id+"F2.wireOp",EDGE,"E43.MirrorCS")])],"isStart":false})});
            var Q39;
            Q39=makeQuery(id+"F10.boolean.opBoolean","COPY",EDGE,{"derivedFrom":makeQuery(id+"F10.opExtrude","CAP_EDGE",EDGE,{"disambiguationData":[OSD([sQuery(id+"F2.wireOp",EDGE,"E33"),sQuery(id+"F2.wireOp",EDGE,"E42.MirrorCS")])],"isStart":false})});
            var Q40;
            Q40=makeQuery(id+"F10.boolean.opBoolean","COPY",EDGE,{"derivedFrom":makeQuery(id+"F10.opExtrude","CAP_EDGE",EDGE,{"disambiguationData":[OSD([sQuery(id+"F2.wireOp",EDGE,"E32")])],"isStart":false})});
            var Q41;
            Q41=makeQuery(id+"F10.boolean.opBoolean","COPY",EDGE,{"derivedFrom":makeQuery(id+"F10.opExtrude","CAP_EDGE",EDGE,{"disambiguationData":[OSD([sQuery(id+"F2.wireOp",EDGE,"E34")])],"isStart":false})});
            var Q42;
            Q42=makeQuery(id+"F10.boolean.opBoolean","COPY",EDGE,{"derivedFrom":makeQuery(id+"F10.opExtrude","CAP_EDGE",EDGE,{"disambiguationData":[OSD([sQuery(id+"F2.wireOp",EDGE,"E50")])],"isStart":true})});
            var Q43;
            Q43=makeQuery(id+"F10.boolean.opBoolean","COPY",EDGE,{"derivedFrom":makeQuery(id+"F10.opExtrude","CAP_EDGE",EDGE,{"disambiguationData":[OSD([sQuery(id+"F2.wireOp",EDGE,"E51.MirrorC")])],"isStart":true})});
            var Q44;
            Q44=makeQuery(id+"F10.boolean.opBoolean","COPY",EDGE,{"derivedFrom":makeQuery(id+"F10.opExtrude","CAP_EDGE",EDGE,{"disambiguationData":[OSD([sQuery(id+"F2.wireOp",EDGE,"E51.MirrorC")])],"isStart":false})});
            var Q45;
            Q45=makeQuery(id+"F10.boolean.opBoolean","COPY",EDGE,{"derivedFrom":makeQuery(id+"F10.opExtrude","CAP_EDGE",EDGE,{"disambiguationData":[OSD([sQuery(id+"F2.wireOp",EDGE,"E50")])],"isStart":false})});
            fillet(context, id + "F14", {"entities" : qUnion([Q0, Q1, Q2, Q3, Q4, Q5, Q6, Q7, Q8, Q9, Q10, Q11, Q12, Q13, Q14, Q15, Q16, Q17, Q18, Q19, Q20, Q21, Q22, Q23, Q24, Q25, Q26, Q27, Q28, Q29, Q30, Q31, Q32, Q33, Q34, Q35, Q36, Q37, Q38, Q39, Q40, Q41, Q42, Q43, Q44, Q45]), "radius" : 1 * mm, "tangentPropagation" : true, "allowEdgeOverflow" : false});
        }
    });
